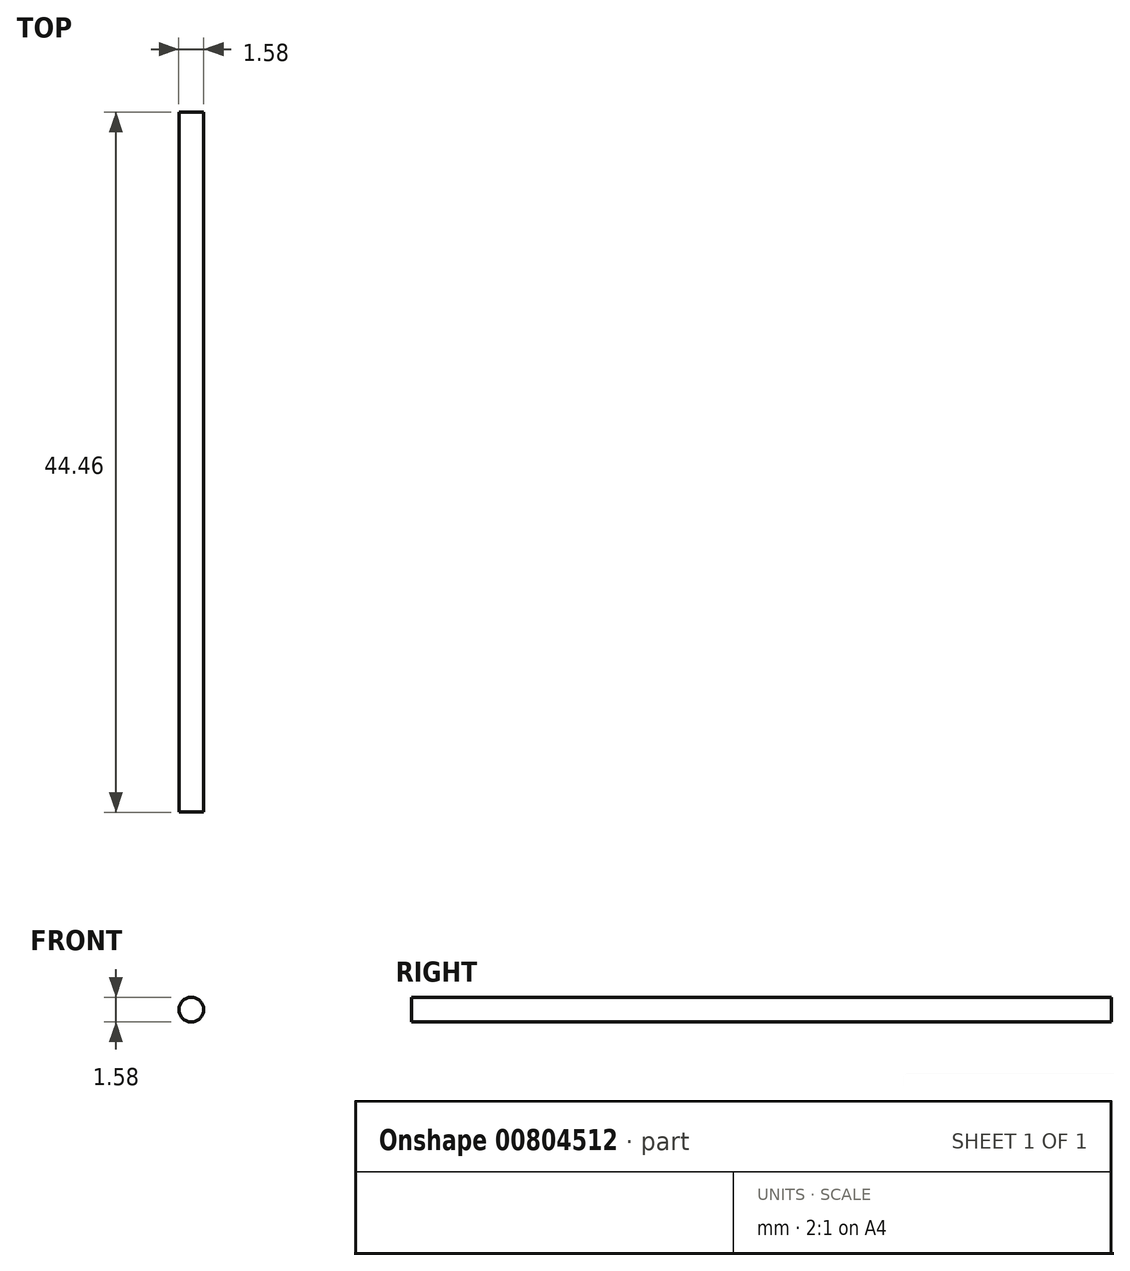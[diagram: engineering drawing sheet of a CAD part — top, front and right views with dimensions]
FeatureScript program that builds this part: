
annotation { "Feature Type Name" : "Feature", "Feature Type Description" : "" }
export const myFeature = defineFeature(function(context is Context, id is Id, definition is map)
    precondition{}
    {
        {
            var Q0;
            Q0=qCreatedBy(makeId("Front.planeOp"),FACE);
            var sketch = newSketch(context, id + "F0", { "sketchPlane" : qUnion([Q0])});
            skCircle(sketch, "E0", {"center": v(0, 0) * mm, "radius": 0.79 * mm});
            skSolve(sketch);
        }
        {
            var Q0;
            Q0 = qSketchRegion(id + "F0", true);
            extrude(context, id + "F1", {"entities" : qUnion([Q0]), "endBound" : BoundingType.SYMMETRIC, "depth" : 44.45 * mm, "offsetDistance" : 25.4 * mm});
        }
    });
